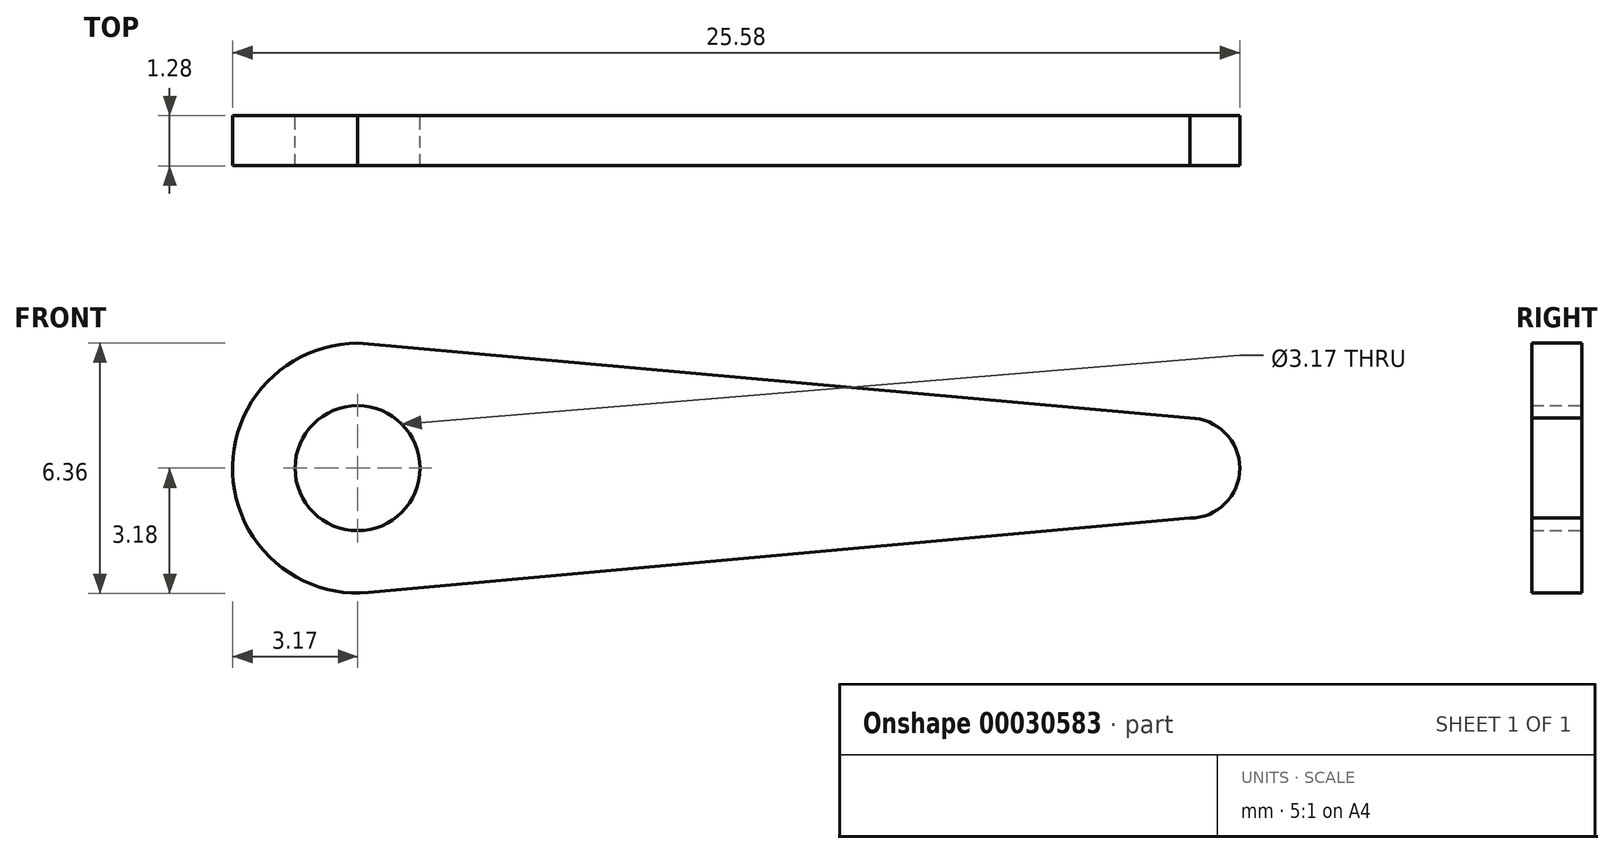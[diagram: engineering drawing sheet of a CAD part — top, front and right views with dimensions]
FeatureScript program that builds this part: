
annotation { "Feature Type Name" : "Feature", "Feature Type Description" : "" }
export const myFeature = defineFeature(function(context is Context, id is Id, definition is map)
    precondition{}
    {
        {
            var Q0;
            Q0=qCreatedBy(makeId("Front.planeOp"),FACE);
            var sketch = newSketch(context, id + "F0", { "sketchPlane" : qUnion([Q0])});
            skLineSegment(sketch, "E0", {"start": v(-12.53, 0) * mm, "end": v(3.17, 0) * mm, "construction": true});
            skLineSegment(sketch, "E1", {"start": v(3.17, 0) * mm, "end": v(-12.53, 0) * mm, "construction": true});
            skCircle(sketch, "E2", {"center": v(0, 0) * mm, "radius": 1.59 * mm});
            skCircle(sketch, "E3", {"center": v(0, 0) * mm, "radius": 3.18 * mm});
            skLineSegment(sketch, "E4", {"start": v(-12.53, 0) * mm, "end": v(-78.75, 0) * mm, "construction": true});
            skLineSegment(sketch, "E5", {"start": v(-78.75, 0) * mm, "end": v(-12.53, 0) * mm, "construction": true});
            skLineSegment(sketch, "E6.trimOffspring", {"start": v(22.41, 0) * mm, "end": v(81, 0) * mm, "construction": true});
            skLineSegment(sketch, "E7.trimOffspring", {"start": v(-3.17, 0) * mm, "end": v(3.17, 0) * mm, "construction": true});
            skLineSegment(sketch, "E8", {"start": v(0, 3.18) * mm, "end": v(21.14, 1.27) * mm});
            skArc(sketch, "E9", {"start": v(21.14, -1.27) * mm, "mid": v(22.41, 0) * mm, "end": v(21.14, 1.27) * mm});
            skLineSegment(sketch, "E10", {"start": v(21.14, -1.27) * mm, "end": v(0, -3.19) * mm});
            skSolve(sketch);
        }
        {
            var Q0;
            {var subQ3=sQuery(id+"F0.wireOp",EDGE,"E9");Q0=makeQuery(id+"F0.imprint","IMPRINT",FACE,{"disambiguationData":[TD([[makeQuery(id+"F0.imprint","IMPRINT",EDGE,{"derivedFrom":subQ3}),1.0]])]});}
            var Q1;
            Q1=makeQuery(id+"F0.imprint","IMPRINT",FACE,{"disambiguationData":[TD([[makeQuery(id+"F0.imprint","IMPRINT",EDGE,{"derivedFrom":sQuery(id+"F0.wireOp",EDGE,"E2")}),-1.0]])]});
            extrude(context, id + "F1", {"entities" : qUnion([Q0, Q1]), "endBound" : BoundingType.SYMMETRIC, "depth" : 1.27 * mm});
        }
    });
